# Revit family: sch-40_50exc_50Hz
name_source: partatom
category: 機械設備
units: mm (PartAtom-declared; Revit-internal decimal feet)

## family parameters
OmniClass タイトル = Heat Exchangers for Ventilation Air
OmniClass 番号 = 23.75.10.34.21
パーツ タイプ = 標準
ロード時にボイドで切り取り = いいえ
丸型コネクタ寸法 = 直径を使用
作業面ベース = いいえ
共有 = いいえ
常に垂直 = はい
部屋計算ポイント = はい

## types (2) — shared parameters
Clearance Bottom = 600  [stored 1.9685 ft]
Clearance Left = 400  [stored 1.31234 ft]
Clearance Right = 400  [stored 1.31234 ft]
Duct_Depth = 85  [stored 0.278871 ft]
Duct_Pitch = 600  [stored 1.9685 ft]
Duct_W = 150
EAサイズ_D = 192  [stored 0.629921 ft]
IfcExportAs = IfcAirToAirHeatRecoveryType
IfcExportType = ROTARYWHEEL
OAサイズ_D = 192  [stored 0.629921 ft]
OmniClassCode = 23-27 23 19 11
URL = https://www.mitsubishielectric.co.jp
Uniclass2015Code = Pr_60_60_36_88
Uniclass2015Title = Thermal wheels
Uniclass2015Version = Systems v1.9
Width = 922  [stored 3.02493 ft]
メンテナンススペース = はい
仕様書バージョン = Version1.0
企業コード = 108420
分類コード = 50052504100060
初期抵抗 = 0.0 Pa
周波数 = 50 Hz
呼称 = 全熱交換ユニット
外気量 = 0.0 m³/h
天吊金具_D = 68
天吊金具ピッチ1 = 845  [stored 2.77231 ft]
実風量 = 0.0 m³/h
形式 = 天吊露出形
排気量 = 0.0 m³/h
本体マテリアル = <カテゴリ別>
極数 = 2
法定耐用年数 = 15
相 = 1
積算_科目 = 1 空気調和設備
符号 = HEU
製品リリース年月 = 2021/4/20
製品出荷対象 = 国内
製造元 = 三菱電機株式会社
設置方法 = 天吊露出形
設計風量 = 0.0 m³/h
説明 = 学校用ロスナイ 天吊露出形
負荷分類 = 3_ファン類
運転質量 = 0.00 kg
電動機出力 = 0 W
電圧 = 100 V
zero-valued in all types: Clearance Top, EAサイズ_W, OAサイズ_W, RAサイズ_D, SAサイズ_D

## per-type parameters (varying)
| type | Depth | Duct_Height | Height | MAX静圧 | MAX風量 | MID静圧 | MID風量 | MIN静圧 | MIN風量 | エンタルピ交換効率_冷房 | エンタルピ交換効率_暖房 | 価格 | 天吊金具ピッチ2 | 機外静圧 | 機外静圧_排気 | 消費電力 | 温度交換効率 | 製品質量 | 質量 | 面風速 | 風量 | 騒音レベル(dB(A)) |
| SCH-40EXC | 693  [stored 2.27362 ft] | 128 | 304  [stored 0.997375 ft] | 40.0 Pa | 400.0 m³/h | 10.0 Pa | 200.0 m³/h | 6.0 Pa | 155.0 m³/h | 40.00% | 45.00% | 314000 $ | 495  [stored 1.62402 ft] | 40.0 Pa | 40.0 Pa | 134 W | 60.00% | 29.00 kg | 34.80 kg | 3.5 m/s | 400.0 m³/h | 39 |
| SCH-50EXC | 900  [stored 2.95276 ft] | 135  [stored 0.442913 ft] | 338  [stored 1.10892 ft] | 60.0 Pa | 500.0 m³/h | 27.0 Pa | 330.0 m³/h | 7.5 Pa | 175.0 m³/h | 58.00% | 62.00% | 372000 $ | 710 | 60.0 Pa | 60.0 Pa | 180 W | 74.00% | 38.00 kg | 45.60 kg | 4.4 m/s | 500.0 m³/h | 39.5 |

note: column(s) folded — value = type name in every type: モデル

note: [stored X ft] marks values corroborated as IEEE doubles in the binary element streams (Revit-internal decimal feet)
